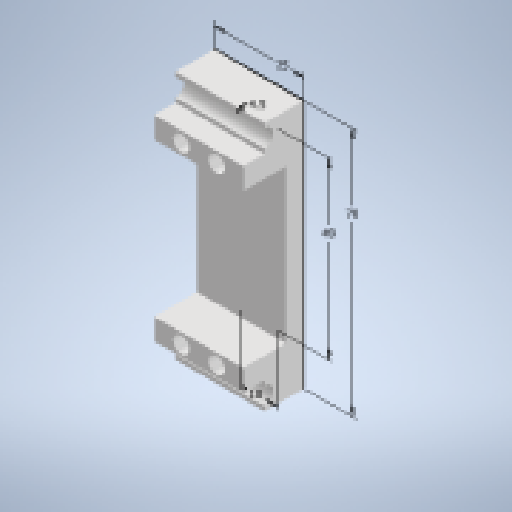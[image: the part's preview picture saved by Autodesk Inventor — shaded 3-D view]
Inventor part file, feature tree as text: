
AUTODESK INVENTOR PART (.ipt)
format: ipt  version: 2025.2 (Build 292293000, 293)  size: 289,280 bytes
history: native  units: mm
features: extrude x3, sketch x2
ambient origin geometry x8: Origin, YZ Plane, XZ Plane, XY Plane, X Axis, Y Axis, Z Axis, Center Point
bodies: Solid1 (feature_tree)
feature tree (5):
  sketch  "Sketch1"  dims[d0=4.5mm d1=10.0mm]
  extrude  "Extrusion1"  Depth=10.0mm
  extrude  "Extrusion2"  Depth=25.0mm
  extrude  "Extrusion3"  Depth=70.0mm
  sketch  "Sketch2"  dims[d2=49.0mm d3=25.0mm d4=70.0mm d5=5.0mm d6=0.0mm d7=6.0mm d8=7.5mm d9=5.0mm d10=5.0mm d11=0.0mm d12=6.0mm d13=12.0mm d14=49.0mm d15=0.0mm]
